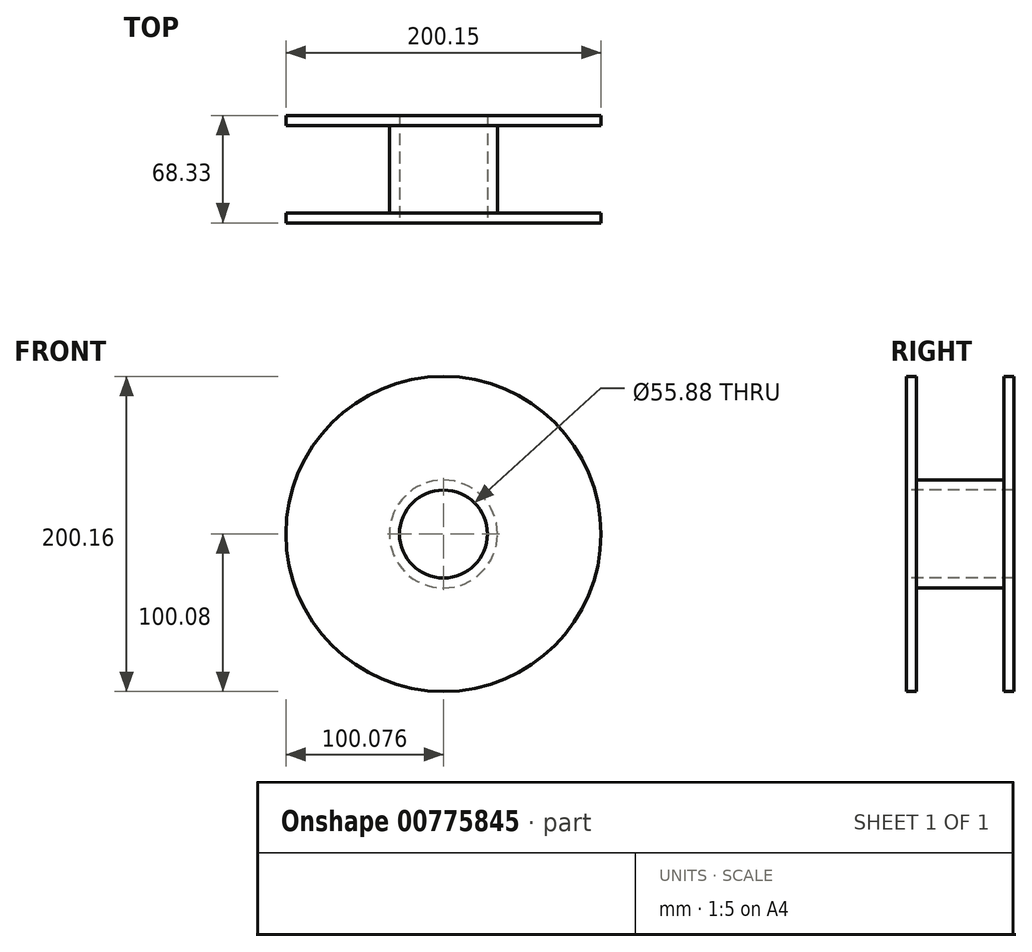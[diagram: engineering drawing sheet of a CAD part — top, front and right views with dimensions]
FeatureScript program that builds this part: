
annotation { "Feature Type Name" : "Feature", "Feature Type Description" : "" }
export const myFeature = defineFeature(function(context is Context, id is Id, definition is map)
    precondition{}
    {
        {
            var Q0;
            Q0=qCreatedBy(makeId("Top.planeOp"),FACE);
            var sketch = newSketch(context, id + "F0", { "sketchPlane" : qUnion([Q0])});
            skLineSegment(sketch, "E0", {"start": v(-62.73, 19.65) * mm, "end": v(37.34, 19.65) * mm});
            skLineSegment(sketch, "E1", {"start": v(-62.73, 19.65) * mm, "end": v(-62.73, 87.98) * mm});
            skLineSegment(sketch, "E2", {"start": v(-62.73, 87.98) * mm, "end": v(37.34, 87.98) * mm});
            skLineSegment(sketch, "E3", {"start": v(37.34, 87.98) * mm, "end": v(37.34, 19.65) * mm});
            skLineSegment(sketch, "E4", {"start": v(-62.73, 19.65) * mm, "end": v(-34.8, 19.65) * mm});
            skLineSegment(sketch, "E5", {"start": v(-62.73, 87.98) * mm, "end": v(-34.8, 87.98) * mm});
            skLineSegment(sketch, "E6", {"start": v(-34.8, 87.98) * mm, "end": v(-34.8, 19.65) * mm});
            skLineSegment(sketch, "E7", {"start": v(-28.44, 81.63) * mm, "end": v(37.34, 81.63) * mm});
            skLineSegment(sketch, "E8", {"start": v(-28.44, 81.63) * mm, "end": v(-28.44, 26) * mm});
            skLineSegment(sketch, "E9", {"start": v(-28.44, 26) * mm, "end": v(37.34, 26) * mm});
            skSolve(sketch);
        }
        {
            var Q0;
            {var subQ7=sQuery(id+"F0.wireOp",EDGE,"E6");Q0=makeQuery(id+"F0.imprint","IMPRINT",FACE,{"disambiguationData":[TD([[makeQuery(id+"F0.imprint","IMPRINT",EDGE,{"derivedFrom":subQ7}),1.0]])]});}
            var Q1;
            Q1=sQuery(id+"F0.wireOp",EDGE,"E1");
            revolve(context, id + "F1", {"surfaceOperationType" : NewSurfaceOperationType.NEW, "entities" : qUnion([Q0]), "axis" : qUnion([Q1]), "revolveType" : RevolveType.FULL});
        }
    });
